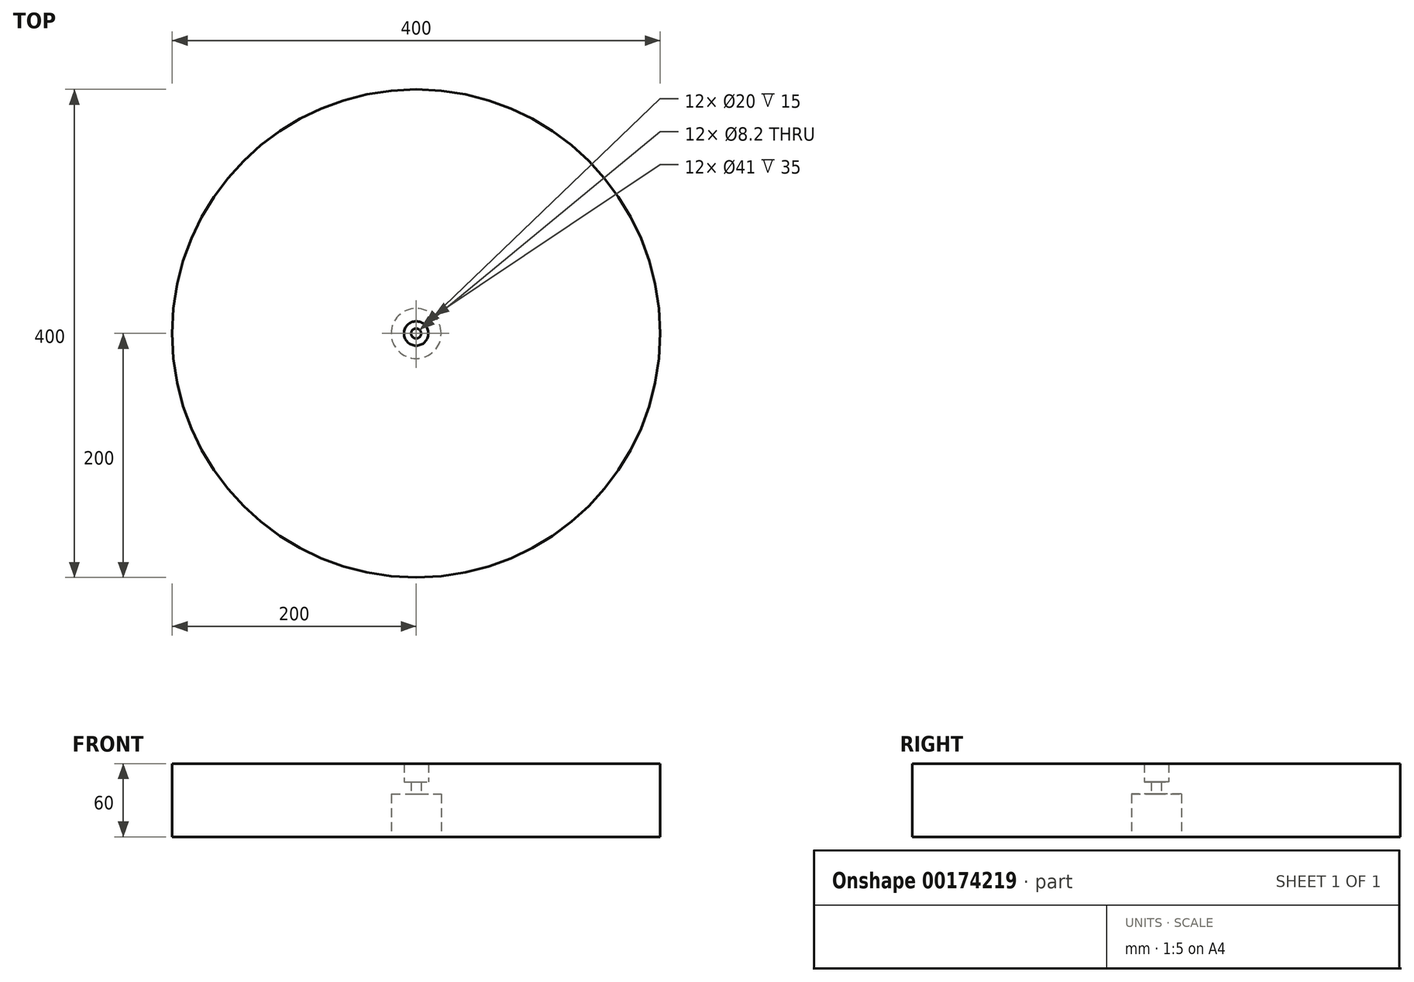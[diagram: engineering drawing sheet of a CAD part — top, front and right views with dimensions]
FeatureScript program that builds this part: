
annotation { "Feature Type Name" : "Feature", "Feature Type Description" : "" }
export const myFeature = defineFeature(function(context is Context, id is Id, definition is map)
    precondition{}
    {
        {
            var Q0;
            Q0=qCreatedBy(makeId("Front.planeOp"),FACE);
            var sketch = newSketch(context, id + "F0", { "sketchPlane" : qUnion([Q0])});
            skLineSegment(sketch, "E0", {"start": v(0, -50) * mm, "end": v(0, 150) * mm});
            skLineSegment(sketch, "E1.trimOffspring", {"start": v(10, 135) * mm, "end": v(10, 150) * mm});
            skLineSegment(sketch, "E2.trimOffspring", {"start": v(10, 150) * mm, "end": v(200, 150) * mm});
            skLineSegment(sketch, "E3.trimOffspring", {"start": v(200, 90) * mm, "end": v(200, 150) * mm});
            skLineSegment(sketch, "E4.trimOffspring", {"start": v(20.5, 90) * mm, "end": v(200, 90) * mm});
            skLineSegment(sketch, "E5.0", {"start": v(20.5, 90) * mm, "end": v(20.5, 125) * mm});
            skLineSegment(sketch, "E6.0", {"start": v(4.1, 125) * mm, "end": v(20.5, 125) * mm});
            skLineSegment(sketch, "E7.trimOffspring", {"start": v(4.1, 125) * mm, "end": v(4.1, 135) * mm});
            skPoint(sketch, "E8.orphan", {"position": v(0, 90) * mm});
            skLineSegment(sketch, "E9.0", {"start": v(4.1, 135) * mm, "end": v(10, 135) * mm});
            skSolve(sketch);
        }
        {
            var Q0;
            Q0=makeQuery(id+"F0.imprint","IMPRINT",FACE,{"disambiguationData":[TD([[makeQuery(id+"F0.imprint","IMPRINT",EDGE,{"derivedFrom":sQuery(id+"F0.wireOp",EDGE,"E1.trimOffspring")}),-1.0]])]});
            var Q1;
            Q1=sQuery(id+"F0.wireOp",EDGE,"E0");
            revolve(context, id + "F1", {"entities" : qUnion([Q0]), "axis" : qUnion([Q1]), "revolveType" : RevolveType.FULL});
        }
    });
